# Revit family: Wall-Panel_Operable-Partition_Moderco_Crystal-Series
name_source: partatom
category: Curtain Panels
units: mm (PartAtom-declared; Revit-internal decimal feet)

## family parameters
Always vertical = Yes
Classification Number = 23.25.40.17
Cut with Voids When Loaded = No
Shared = No

## types (1)
- as Specified
    Assembly Code = C1010300
    Construction Details = http://www.arcat.com
    Description = Moderco Crystal Series Wall Panel as Specified
    Expected Lifespan (Years) = 0
    Glazing Thickness = 0' - 0 1/4"
    Keynote = 10 22 26
    Maintenance Schedule (Months) = 0
    Manufacturer = Moderco, Inc
    Manufacturer Fax = 450-641-4965 or 800-231-4965
    Manufacturer Website = http://moderco.com
    Max Height = 12' - 0"
    Model = Crystal
    Panel Thickness = 0' - 4"
    Product Data = http://www.arcat.com
    Revision = R1_2015-09
    Sales Information = http://moderco.com
    Specification = http://www.arcat.com
    Type Comments = Glazing is not included with the Wall Panel.
    URL = http://moderco.com
    Use = Single
    Warranty Duration (Years) = 0

## geometry (parser evidence)
native form markers: Sweep x3
no freeform markers — native parametric forms only
